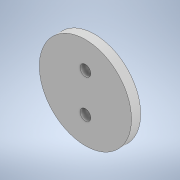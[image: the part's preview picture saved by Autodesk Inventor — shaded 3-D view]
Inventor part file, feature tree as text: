
AUTODESK INVENTOR PART (.ipt)
format: ipt  version: 2020 (Build 240168000, 168)  size: 103,424 bytes
history: native  units: mm
features: extrude x1, sketch x1
ambient origin geometry x8: Origin, YZ Plane, XZ Plane, XY Plane, X Axis, Y Axis, Z Axis, Center Point
bodies: 实体1 (feature_tree)
feature tree (2):
  extrude  "拉伸1"  Depth=6.0mm
  sketch  "草图1"  dims[d0=60.0mm d1=7.0mm d2=7.0mm d3=25.0mm d4=6.0mm d5=0.0mm]
